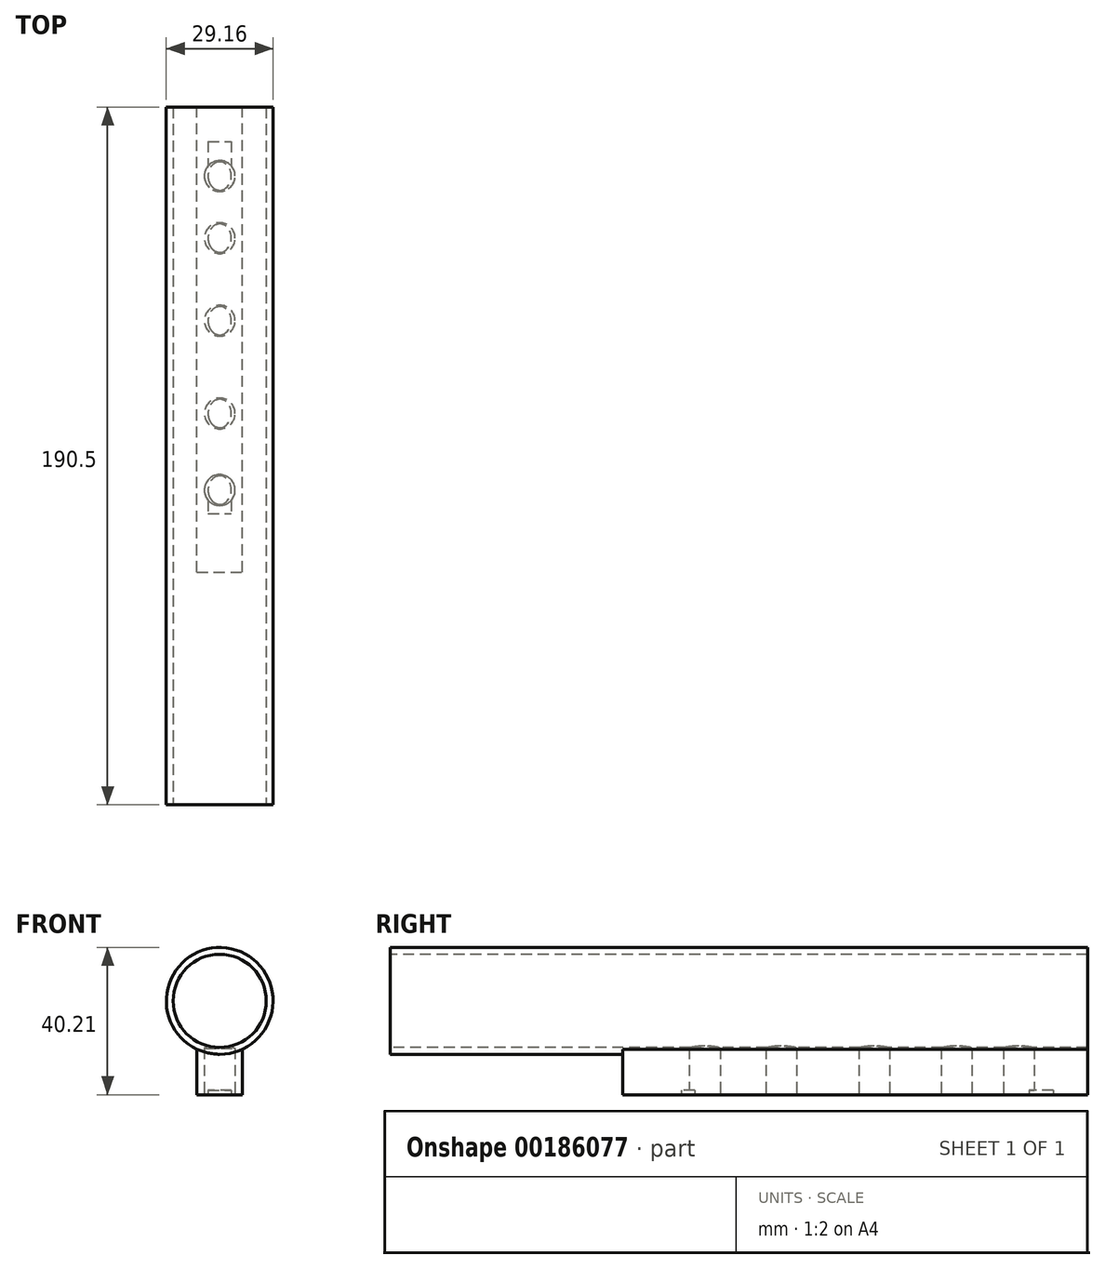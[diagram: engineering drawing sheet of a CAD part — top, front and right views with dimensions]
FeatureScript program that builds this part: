
annotation { "Feature Type Name" : "Feature", "Feature Type Description" : "" }
export const myFeature = defineFeature(function(context is Context, id is Id, definition is map)
    precondition{}
    {
        {
            var Q0;
            Q0=qCreatedBy(makeId("Front.planeOp"),FACE);
            var sketch = newSketch(context, id + "F0", { "sketchPlane" : qUnion([Q0])});
            skCircle(sketch, "E0", {"center": v(0, 0) * mm, "radius": 14.58 * mm});
            skLineSegment(sketch, "E1.top", {"start": v(-6.22, -25.63) * mm, "end": v(6.22, -25.63) * mm});
            skLineSegment(sketch, "E1.left", {"start": v(-6.22, -13.18) * mm, "end": v(-6.22, -25.63) * mm});
            skLineSegment(sketch, "E1.right", {"start": v(6.22, -13.18) * mm, "end": v(6.22, -25.63) * mm});
            skPoint(sketch, "E1.middle", {"position": v(0, -19.4) * mm});
            skSolve(sketch);
        }
        {
            var Q0;
            {var subQ0=sQuery(id+"F0.wireOp",EDGE,"E0");var subQ1=makeQuery(id+"F0.imprint","INTERSECT",VERTEX,{"derivedFrom":[subQ0,sQuery(id+"F0.wireOp",EDGE,"E1.left")]});Q0=makeQuery(id+"F0.imprint","IMPRINT",FACE,{"disambiguationData":[TD([[makeQuery(id+"F0.imprint","IMPRINT",EDGE,{"disambiguationData":[TD([[subQ1,-1.0]])],"derivedFrom":subQ0}),1.0]])]});}
            extrude(context, id + "F1", {"entities" : qUnion([Q0]), "depth" : 190.5 * mm});
        }
        {
            var Q0;
            Q0=makeQuery(id+"F0.imprint","IMPRINT",FACE,{"disambiguationData":[TD([[makeQuery(id+"F0.imprint","IMPRINT",EDGE,{"derivedFrom":sQuery(id+"F0.wireOp",EDGE,"E1.top")}),1.0]])]});
            extrude(context, id + "F2", {"entities" : qUnion([Q0]), "operationType" : NewBodyOperationType.ADD, "depth" : 127 * mm});
        }
        {
            var Q0;
            Q0=makeQuery(id+"F1.opExtrude","CAP_FACE",FACE,{"disambiguationData":[OSD([sQuery(id+"F0.wireOp",EDGE,"E0")])],"isStart":false});
            var sketch = newSketch(context, id + "F3", { "sketchPlane" : qUnion([Q0])});
            skCircle(sketch, "E2", {"center": v(0, 0) * mm, "radius": 12.73 * mm});
            skSolve(sketch);
        }
        {
            var Q0;
            Q0=makeQuery(id+"F3.imprint","IMPRINT",FACE,{"disambiguationData":[TD([[makeQuery(id+"F3.imprint","IMPRINT",EDGE,{"derivedFrom":sQuery(id+"F3.wireOp",EDGE,"E2")}),1.0]])]});
            extrude(context, id + "F4", {"entities" : qUnion([Q0]), "operationType" : NewBodyOperationType.REMOVE, "endBound" : BoundingType.UP_TO_NEXT, "oppositeDirection" : true, "depth" : 25.4 * mm});
        }
        {
            var Q0;
            Q0=makeQuery(id+"F2.opExtrude","SWEPT_FACE",FACE,{"disambiguationData":[OSD([sQuery(id+"F0.wireOp",EDGE,"E1.top")])]});
            var sketch = newSketch(context, id + "F5", { "sketchPlane" : qUnion([Q0])});
            skPoint(sketch, "E3", {"position": v(0, 18.83) * mm});
            skPoint(sketch, "E4", {"position": v(0, 35.8) * mm});
            skPoint(sketch, "E5", {"position": v(0, 58.34) * mm});
            skPoint(sketch, "E6", {"position": v(0, 83.67) * mm});
            skPoint(sketch, "E7", {"position": v(0, 104.59) * mm});
            skSolve(sketch);
        }
        {
            var Q0;
            Q0=sQuery(id+"F5.wireOp",VERTEX,"E3");
            var Q1;
            Q1=sQuery(id+"F5.wireOp",VERTEX,"E4");
            var Q2;
            Q2=sQuery(id+"F5.wireOp",VERTEX,"E5");
            var Q3;
            Q3=sQuery(id+"F5.wireOp",VERTEX,"E6");
            var Q4;
            Q4=sQuery(id+"F5.wireOp",VERTEX,"E7");
            var Q5;
            Q5=makeQuery(id+"F1.opExtrude","SWEPT_BODY",BODY,{"disambiguationData":[OSD([sQuery(id+"F0.wireOp",EDGE,"E0")])]});
            hole(context, id + "F6", {"style" : HoleStyle.SIMPLE, "endStyle" : HoleEndStyle.BLIND, "standardTappedOrClearance" : lookupTablePath({ "standard" : "ANSI", "fit" : "Normal (ASME)", "size" : "5/16", "type" : "Clearance" }), "standardBlindInLast" : lookupTablePath({ "fit" : "Free", "standard" : "ANSI", "size" : "5/16", "type" : "Clearance" }), "holeDiameter" : 8.43 * mm, "holeDepth" : 12.7 * mm, "locations" : qUnion([Q0, Q1, Q2, Q3, Q4]), "scope" : qUnion([Q5])});
        }
        {
            var Q0;
            Q0=makeQuery(id+"F2.opExtrude","SWEPT_FACE",FACE,{"disambiguationData":[OSD([sQuery(id+"F0.wireOp",EDGE,"E1.top")])]});
            var sketch = newSketch(context, id + "F7", { "sketchPlane" : qUnion([Q0])});
            skLineSegment(sketch, "E8.bottom", {"start": v(-3.17, 9.39) * mm, "end": v(3.18, 9.39) * mm});
            skLineSegment(sketch, "E8.top", {"start": v(-3.18, 110.99) * mm, "end": v(3.17, 110.99) * mm});
            skLineSegment(sketch, "E8.left", {"start": v(-3.17, 9.39) * mm, "end": v(-3.18, 110.99) * mm});
            skLineSegment(sketch, "E8.right", {"start": v(3.18, 9.39) * mm, "end": v(3.17, 110.99) * mm});
            skPoint(sketch, "E8.middle", {"position": v(0, 60.19) * mm});
            skSolve(sketch);
        }
        {
            var Q0;
            {var subQ0=sQuery(id+"F7.wireOp",EDGE,"E8.left");var subQ1=makeQuery(id+"F6.hole-3.boolean.opBoolean","COPY",EDGE,{"derivedFrom":makeQuery(id+"F6.hole-3.opRevolve","SWEPT_EDGE",EDGE,{"disambiguationData":[OSD([sQuery(id+"F6.hole-3.sketch.wireOp",EDGE,"core_line_2"),sQuery(id+"F6.hole-3.sketch.wireOp",EDGE,"core_line_3")])]})});var subQ2=makeQuery(id+"F7.imprint","INTERSECT",VERTEX,{"disambiguationData":[OD(1.0)],"derivedFrom":[subQ1,subQ0]});Q0=makeQuery(id+"F7.imprint","IMPRINT",FACE,{"disambiguationData":[TD([[makeQuery(id+"F7.imprint","IMPRINT",EDGE,{"disambiguationData":[TD([[subQ2,-1.0]])],"derivedFrom":subQ0}),-1.0]])]});}
            var Q1;
            {var subQ0=sQuery(id+"F7.wireOp",EDGE,"E8.top");Q1=makeQuery(id+"F7.imprint","IMPRINT",FACE,{"disambiguationData":[TD([[makeQuery(id+"F7.imprint","IMPRINT",EDGE,{"derivedFrom":subQ0}),-1.0]])]});}
            var Q2;
            {var subQ0=sQuery(id+"F7.wireOp",EDGE,"E8.left");var subQ1=makeQuery(id+"F6.hole-2.boolean.opBoolean","COPY",EDGE,{"derivedFrom":makeQuery(id+"F6.hole-2.opRevolve","SWEPT_EDGE",EDGE,{"disambiguationData":[OSD([sQuery(id+"F6.hole-2.sketch.wireOp",EDGE,"core_line_2"),sQuery(id+"F6.hole-2.sketch.wireOp",EDGE,"core_line_3")])]})});var subQ2=makeQuery(id+"F7.imprint","INTERSECT",VERTEX,{"disambiguationData":[OD(1.0)],"derivedFrom":[subQ1,subQ0]});Q2=makeQuery(id+"F7.imprint","IMPRINT",FACE,{"disambiguationData":[TD([[makeQuery(id+"F7.imprint","IMPRINT",EDGE,{"disambiguationData":[TD([[subQ2,-1.0]])],"derivedFrom":subQ0}),-1.0]])]});}
            var Q3;
            {var subQ0=sQuery(id+"F7.wireOp",EDGE,"E8.left");var subQ1=makeQuery(id+"F6.hole-1.boolean.opBoolean","COPY",EDGE,{"derivedFrom":makeQuery(id+"F6.hole-1.opRevolve","SWEPT_EDGE",EDGE,{"disambiguationData":[OSD([sQuery(id+"F6.hole-1.sketch.wireOp",EDGE,"core_line_2"),sQuery(id+"F6.hole-1.sketch.wireOp",EDGE,"core_line_3")])]})});var subQ2=makeQuery(id+"F7.imprint","INTERSECT",VERTEX,{"disambiguationData":[OD(1.0)],"derivedFrom":[subQ1,subQ0]});Q3=makeQuery(id+"F7.imprint","IMPRINT",FACE,{"disambiguationData":[TD([[makeQuery(id+"F7.imprint","IMPRINT",EDGE,{"disambiguationData":[TD([[subQ2,-1.0]])],"derivedFrom":subQ0}),-1.0]])]});}
            var Q4;
            {var subQ0=sQuery(id+"F7.wireOp",EDGE,"E8.left");var subQ1=makeQuery(id+"F6.hole-0.boolean.opBoolean","COPY",EDGE,{"derivedFrom":makeQuery(id+"F6.hole-0.opRevolve","SWEPT_EDGE",EDGE,{"disambiguationData":[OSD([sQuery(id+"F6.hole-0.sketch.wireOp",EDGE,"core_line_2"),sQuery(id+"F6.hole-0.sketch.wireOp",EDGE,"core_line_3")])]})});var subQ2=makeQuery(id+"F7.imprint","INTERSECT",VERTEX,{"disambiguationData":[OD(1.0)],"derivedFrom":[subQ1,subQ0]});Q4=makeQuery(id+"F7.imprint","IMPRINT",FACE,{"disambiguationData":[TD([[makeQuery(id+"F7.imprint","IMPRINT",EDGE,{"disambiguationData":[TD([[subQ2,-1.0]])],"derivedFrom":subQ0}),-1.0]])]});}
            var Q5;
            {var subQ0=sQuery(id+"F7.wireOp",EDGE,"E8.bottom");Q5=makeQuery(id+"F7.imprint","IMPRINT",FACE,{"disambiguationData":[TD([[makeQuery(id+"F7.imprint","IMPRINT",EDGE,{"derivedFrom":subQ0}),1.0]])]});}
            extrude(context, id + "F8", {"entities" : qUnion([Q0, Q1, Q2, Q3, Q4, Q5]), "operationType" : NewBodyOperationType.REMOVE, "oppositeDirection" : true, "depth" : 1.27 * mm});
        }
    });
